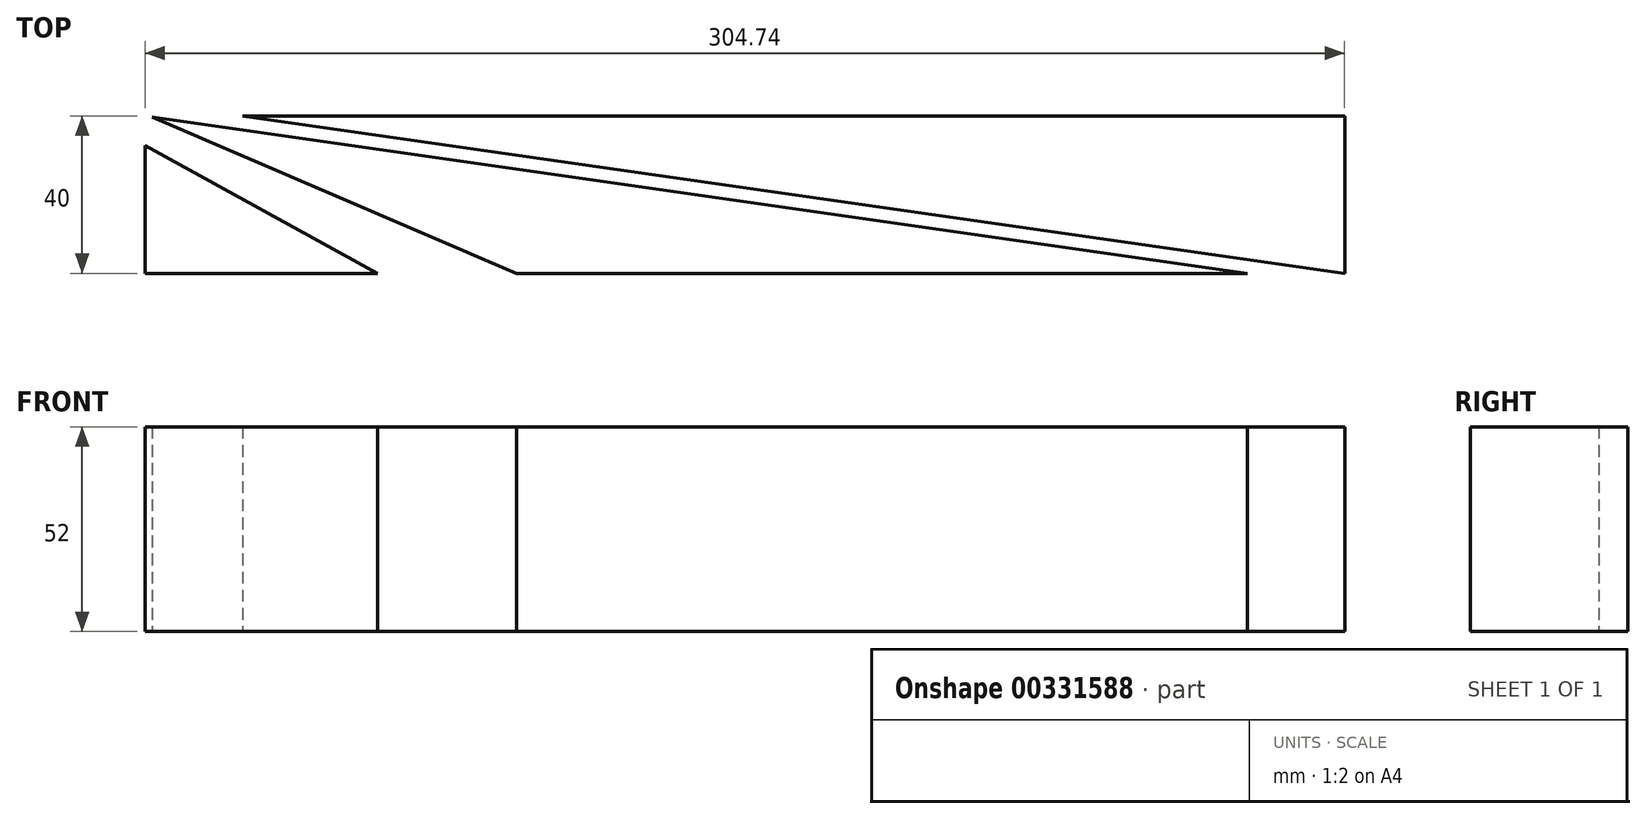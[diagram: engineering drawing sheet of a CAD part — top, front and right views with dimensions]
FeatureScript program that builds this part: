
annotation { "Feature Type Name" : "Feature", "Feature Type Description" : "" }
export const myFeature = defineFeature(function(context is Context, id is Id, definition is map)
    precondition{}
    {
        {
            var Q0;
            Q0=qCreatedBy(makeId("Top.planeOp"),FACE);
            var sketch = newSketch(context, id + "F0", { "sketchPlane" : qUnion([Q0])});
            skLineSegment(sketch, "E0.bottom", {"start": v(152.37, -20) * mm, "end": v(-152.37, -20) * mm});
            skLineSegment(sketch, "E0.top", {"start": v(152.37, 20) * mm, "end": v(-152.37, 20) * mm});
            skLineSegment(sketch, "E0.left", {"start": v(152.37, -20) * mm, "end": v(152.37, 20) * mm});
            skLineSegment(sketch, "E0.right", {"start": v(-152.37, -20) * mm, "end": v(-152.37, 20) * mm});
            skPoint(sketch, "E0.middle", {"position": v(0, 0) * mm});
            skLineSegment(sketch, "E1", {"start": v(-152.37, 20) * mm, "end": v(151.88, -23.46) * mm});
            skLineSegment(sketch, "E2", {"start": v(151.88, -23.46) * mm, "end": v(152.37, -20) * mm});
            skLineSegment(sketch, "E3", {"start": v(152.37, -20) * mm, "end": v(-151.88, 23.46) * mm});
            skLineSegment(sketch, "E4", {"start": v(-151.88, 23.46) * mm, "end": v(-152.37, 20) * mm});
            skPoint(sketch, "E5", {"position": v(127.63, -20) * mm});
            skSolve(sketch);
        }
        {
            var Q0;
            {var subQ0=sQuery(id+"F0.wireOp",EDGE,"E0.right");Q0=makeQuery(id+"F0.imprint","IMPRINT",FACE,{"disambiguationData":[TD([[makeQuery(id+"F0.imprint","IMPRINT",EDGE,{"derivedFrom":subQ0}),-1.0]])]});}
            var Q1;
            {var subQ0=sQuery(id+"F0.wireOp",EDGE,"E0.left");Q1=makeQuery(id+"F0.imprint","IMPRINT",FACE,{"disambiguationData":[TD([[makeQuery(id+"F0.imprint","IMPRINT",EDGE,{"derivedFrom":subQ0}),1.0]])]});}
            extrude(context, id + "F1", {"entities" : qUnion([Q0, Q1]), "depth" : 52 * mm});
        }
        {
            var Q0;
            Q0=makeQuery(id+"F1.opExtrude","CAP_FACE",FACE,{"disambiguationData":[OSD([sQuery(id+"F0.wireOp",EDGE,"E0.bottom"),sQuery(id+"F0.wireOp",EDGE,"E0.right"),sQuery(id+"F0.wireOp",EDGE,"E1")])],"isStart":false});
            var sketch = newSketch(context, id + "F2", { "sketchPlane" : qUnion([Q0])});
            skLineSegment(sketch, "E6", {"start": v(-58.02, -20) * mm, "end": v(-218.37, 48.88) * mm});
            skLineSegment(sketch, "E7", {"start": v(-93.29, -20) * mm, "end": v(-58.02, -20) * mm});
            skLineSegment(sketch, "E8", {"start": v(-93.29, -20) * mm, "end": v(-218.37, 48.88) * mm});
            skSolve(sketch);
        }
        {
            var Q0;
            Q0 = qSketchRegion(id + "F2", true);
            extrude(context, id + "F3", {"entities" : qUnion([Q0]), "operationType" : NewBodyOperationType.REMOVE, "endBound" : BoundingType.THROUGH_ALL, "oppositeDirection" : true, "depth" : 25 * mm});
        }
    });
